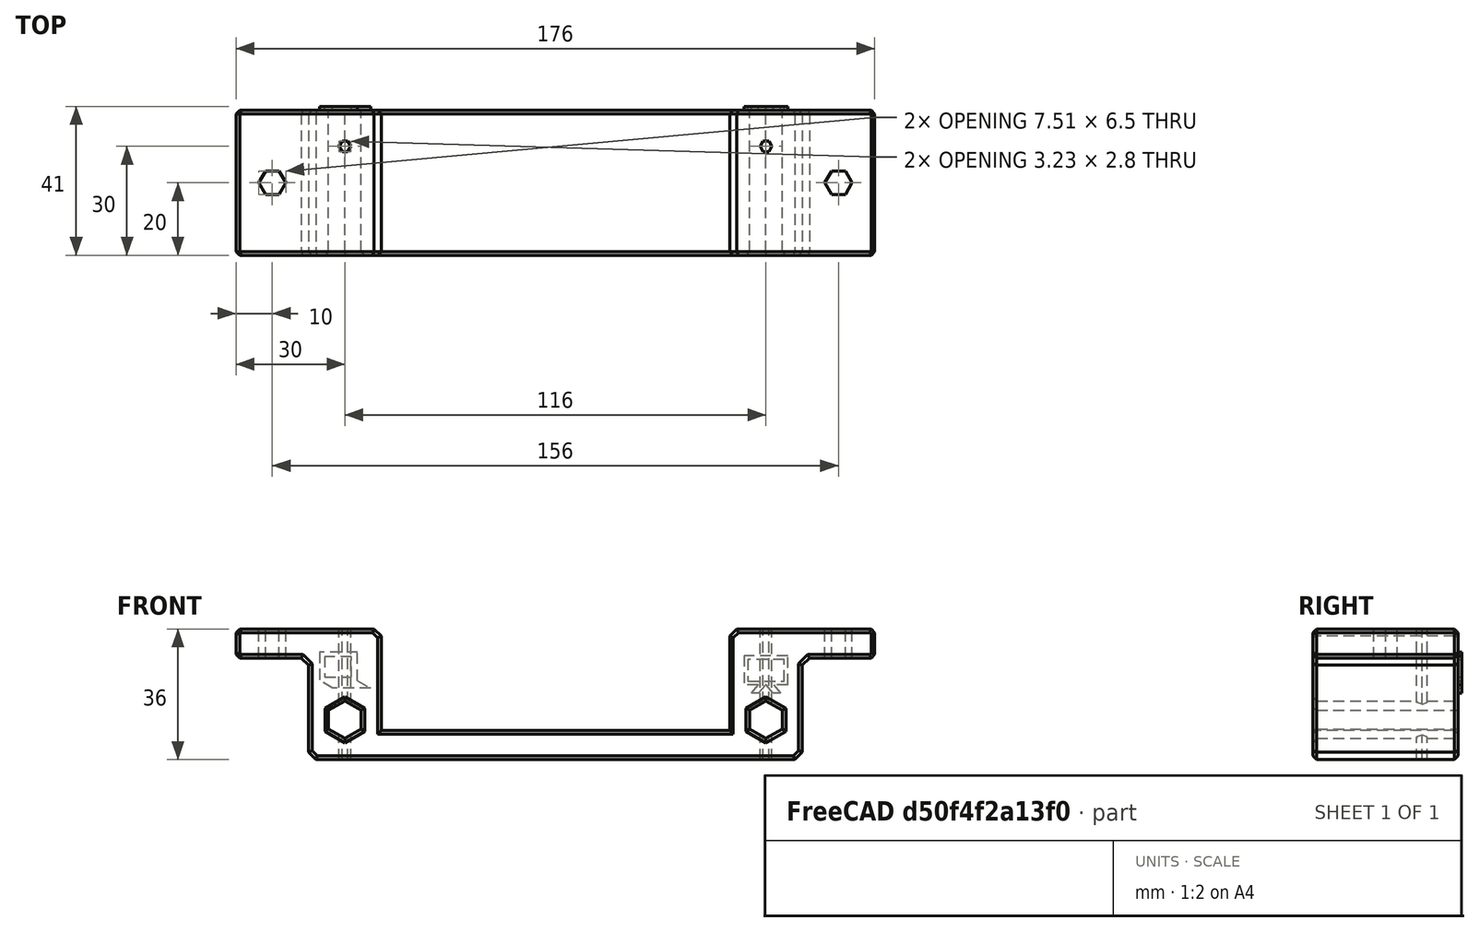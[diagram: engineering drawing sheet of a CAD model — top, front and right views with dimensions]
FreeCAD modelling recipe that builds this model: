
FCSTD DOCUMENT  (FreeCAD 0.19R)
Label: AmpClip
License: All rights reserved
LicenseURL: http://en.wikipedia.org/wiki/All_rights_reserved
objects: PartDesign::Chamfer×5, Sketcher::SketchObject×4, PartDesign::Pad×2, PartDesign::Pocket×2, PartDesign::Body×1, Mesh::Feature×1
note: 23 computed .brp shape members not serialized (recipe doc carries the construction recipe); baked Part::Feature solids carry a one-line shape summary decoded from their .brp

FEATURE [Sketcher::SketchObject] Sketch
  FullyConstrained = true
  MapMode = 5
  Placement = pos=(0,0,0) rot=(1,0,0;1.5708rad)
  Support = -> [XZ_Plane]
  sketch-geometry (12):
    g0: LineSegment StartX=-48 StartY=0 StartZ=0 EndX=-48 EndY=-28 EndZ=0
    g1: LineSegment StartX=-48 StartY=-28 StartZ=0 EndX=48 EndY=-28 EndZ=0
    g2: LineSegment StartX=48 StartY=-28 StartZ=0 EndX=48 EndY=0 EndZ=0
    g3: LineSegment StartX=48 StartY=0 StartZ=0 EndX=88 EndY=0 EndZ=0
    g4: LineSegment StartX=88 StartY=0 StartZ=0 EndX=88 EndY=-8 EndZ=0
    g5: LineSegment StartX=88 StartY=-8 StartZ=0 EndX=68 EndY=-8 EndZ=0
    g6: LineSegment StartX=68 StartY=-8 StartZ=0 EndX=68 EndY=-36 EndZ=0
    g7: LineSegment StartX=68 StartY=-36 StartZ=0 EndX=-68 EndY=-36 EndZ=0
    g8: LineSegment StartX=-68 StartY=-36 StartZ=0 EndX=-68 EndY=-8 EndZ=0
    g9: LineSegment StartX=-68 StartY=-8 StartZ=0 EndX=-88 EndY=-8 EndZ=0
    g10: LineSegment StartX=-88 StartY=-8 StartZ=0 EndX=-88 EndY=-9e-16 EndZ=0
    g11: LineSegment StartX=-88 StartY=-9e-16 StartZ=0 EndX=-48 EndY=0 EndZ=0
  constraints (32):
    c: PointOnObject(g0,g-1)
    c: Coincident(g0,g1)
    c: Horizontal(g1)
    c: Coincident(g1,g2)
    c: Vertical(g2)
    c: Coincident(g2,g3)
    c: Horizontal(g3)
    c: Coincident(g3,g4)
    c: Coincident(g4,g5)
    c: Horizontal(g5)
    c: Coincident(g5,g6)
    c: Vertical(g6)
    c: Coincident(g6,g7)
    c: Coincident(g7,g8)
    c: Coincident(g8,g9)
    c: Coincident(g9,g10)
    c: Coincident(g10,g11)
    c: Coincident(g11,g0)
    c: Horizontal(g9)
    c: Vertical(g10)
    c: Vertical(g4)
    c: Vertical(g0)
    c: Symmetric(g0,g2,g-1)
    c: Symmetric(g6,g7,g-2)
    c: Symmetric(g5,g8,g-2)
    c: Symmetric(g3,g10,g-2)
    c: Distance(g1) = 96
    c: Distance(g5,g2) = 20
    c: Distance(g4) = 8
    c: Distance(g6,g1) = 8
    c: Distance(g5) = 20
    c: Distance(g2) = 28
FEATURE [PartDesign::Pad] Pad
  Direction = (1,1,1)
  Length = 40
  Length2 = 100
  Placement = pos=(0,0,0) rot=(1,0,0;1.5708rad)
  Profile = -> Sketch
  Type = 0
FEATURE [Sketcher::SketchObject] Sketch001
  FullyConstrained = true
  MapMode = 5
  Placement = pos=(0,-40,2.66e-14) rot=(1,0,0;1.5708rad)
  Support = -> [Pad]
  sketch-geometry (14):
    g0: LineSegment StartX=62.5 StartY=-27.5981 StartZ=0 EndX=62.5 EndY=-22.4019 EndZ=0
    g1: LineSegment StartX=62.5 StartY=-22.4019 StartZ=0 EndX=58 EndY=-19.8038 EndZ=0
    g2: LineSegment StartX=58 StartY=-19.8038 StartZ=0 EndX=53.5 EndY=-22.4019 EndZ=0
    g3: LineSegment StartX=53.5 StartY=-22.4019 StartZ=0 EndX=53.5 EndY=-27.5981 EndZ=0
    g4: LineSegment StartX=53.5 StartY=-27.5981 StartZ=0 EndX=58 EndY=-30.1962 EndZ=0
    g5: LineSegment StartX=58 StartY=-30.1962 StartZ=0 EndX=62.5 EndY=-27.5981 EndZ=0
    g6: Circle CenterX=58 CenterY=-25 CenterZ=0 NormalX=0 NormalY=0 NormalZ=1 AngleXU=0 Radius=5.19615
    g7: LineSegment StartX=-58 StartY=-30.1962 StartZ=0 EndX=-53.5 EndY=-27.5981 EndZ=0
    g8: LineSegment StartX=-53.5 StartY=-27.5981 StartZ=0 EndX=-53.5 EndY=-22.4019 EndZ=0
    g9: LineSegment StartX=-53.5 StartY=-22.4019 StartZ=0 EndX=-58 EndY=-19.8038 EndZ=0
    g10: LineSegment StartX=-58 StartY=-19.8038 StartZ=0 EndX=-62.5 EndY=-22.4019 EndZ=0
    g11: LineSegment StartX=-62.5 StartY=-22.4019 StartZ=0 EndX=-62.5 EndY=-27.5981 EndZ=0
    g12: LineSegment StartX=-62.5 StartY=-27.5981 StartZ=0 EndX=-58 EndY=-30.1962 EndZ=0
    g13: Circle CenterX=-58 CenterY=-25 CenterZ=0 NormalX=0 NormalY=0 NormalZ=1 AngleXU=0 Radius=5.19615
  constraints (33):
    c: Coincident(g0,g1)
    c: Coincident(g1,g2)
    c: Coincident(g2,g3)
    c: Coincident(g3,g4)
    c: Coincident(g4,g5)
    c: Coincident(g5,g0)
    c: Equal(g0, g1-g5) x5
    c: PointOnObject(g0,g6)
    c: PointOnObject(g1,g6)
    c: PointOnObject(g2,g6)
    c: PointOnObject(g3,g6)
    c: PointOnObject(g4,g6)
    c: PointOnObject(g5,g6)
    c: Coincident(g7,g8)
    c: Coincident(g8,g9)
    c: Coincident(g9,g10)
    c: Coincident(g10,g11)
    c: Coincident(g11,g12)
    c: Coincident(g12,g7)
    c: Equal(g7, g8-g12) x5
    c: PointOnObject(g7,g13)
    c: PointOnObject(g8,g13)
    c: PointOnObject(g9,g13)
    c: PointOnObject(g10,g13)
    c: PointOnObject(g11,g13)
    c: PointOnObject(g12,g13)
    c: Distance(g7,g9) = 9
    c: Symmetric(g6,g13,g-2)
    c: Distance(g1,g3) = 9
    c: DistanceX(g6) = 58
    c: Vertical(g3)
    c: Vertical(g8)
    c: DistanceY(g6) = -25
FEATURE [PartDesign::Pocket] Pocket
  BaseFeature = -> Pad
  Length = 5
  Length2 = 100
  Placement = pos=(0,0,0) rot=(1,0,0;1.5708rad)
  Profile = -> Sketch001
  Type = 1
FEATURE [Sketcher::SketchObject] Sketch002
  FullyConstrained = true
  MapMode = 5
  Placement = pos=(0,-4e-14,-36) rot=(1,0,0;3.14159rad)
  Support = -> [Pocket]
  sketch-geometry (28):
    g0: LineSegment StartX=-57.1917 StartY=8.6 StartZ=0 EndX=-56.3834 EndY=10 EndZ=0
    g1: LineSegment StartX=-56.3834 StartY=10 StartZ=0 EndX=-57.1917 EndY=11.4 EndZ=0
    g2: LineSegment StartX=-57.1917 StartY=11.4 StartZ=0 EndX=-58.8083 EndY=11.4 EndZ=0
    g3: LineSegment StartX=-58.8083 StartY=11.4 StartZ=0 EndX=-59.6166 EndY=10 EndZ=0
    g4: LineSegment StartX=-59.6166 StartY=10 StartZ=0 EndX=-58.8083 EndY=8.6 EndZ=0
    g5: LineSegment StartX=-58.8083 StartY=8.6 StartZ=0 EndX=-57.1917 EndY=8.6 EndZ=0
    g6: Circle CenterX=-58 CenterY=10 CenterZ=0 NormalX=0 NormalY=0 NormalZ=1 AngleXU=0 Radius=1.61658
    g7: LineSegment StartX=58.8083 StartY=8.6 StartZ=0 EndX=59.6166 EndY=10 EndZ=0
    g8: LineSegment StartX=59.6166 StartY=10 StartZ=0 EndX=58.8083 EndY=11.4 EndZ=0
    g9: LineSegment StartX=58.8083 StartY=11.4 StartZ=0 EndX=57.1917 EndY=11.4 EndZ=0
    g10: LineSegment StartX=57.1917 StartY=11.4 StartZ=0 EndX=56.3834 EndY=10 EndZ=0
    g11: LineSegment StartX=56.3834 StartY=10 StartZ=0 EndX=57.1917 EndY=8.6 EndZ=0
    g12: LineSegment StartX=57.1917 StartY=8.6 StartZ=0 EndX=58.8083 EndY=8.6 EndZ=0
    g13: Circle CenterX=58 CenterY=10 CenterZ=0 NormalX=0 NormalY=0 NormalZ=1 AngleXU=0 Radius=1.61658
    g14: LineSegment StartX=-76.1236 StartY=16.75 StartZ=0 EndX=-74.2472 EndY=20 EndZ=0
    g15: LineSegment StartX=-74.2472 StartY=20 StartZ=0 EndX=-76.1236 EndY=23.25 EndZ=0
    g16: LineSegment StartX=-76.1236 StartY=23.25 StartZ=0 EndX=-79.8764 EndY=23.25 EndZ=0
    g17: LineSegment StartX=-79.8764 StartY=23.25 StartZ=0 EndX=-81.7528 EndY=20 EndZ=0
    g18: LineSegment StartX=-81.7528 StartY=20 StartZ=0 EndX=-79.8764 EndY=16.75 EndZ=0
    g19: LineSegment StartX=-79.8764 StartY=16.75 StartZ=0 EndX=-76.1236 EndY=16.75 EndZ=0
    g20: Circle CenterX=-78 CenterY=20 CenterZ=0 NormalX=0 NormalY=0 NormalZ=1 AngleXU=0 Radius=3.75278
    g21: LineSegment StartX=79.8764 StartY=16.75 StartZ=0 EndX=81.7528 EndY=20 EndZ=0
    g22: LineSegment StartX=81.7528 StartY=20 StartZ=0 EndX=79.8764 EndY=23.25 EndZ=0
    g23: LineSegment StartX=79.8764 StartY=23.25 StartZ=0 EndX=76.1236 EndY=23.25 EndZ=0
    g24: LineSegment StartX=76.1236 StartY=23.25 StartZ=0 EndX=74.2472 EndY=20 EndZ=0
    g25: LineSegment StartX=74.2472 StartY=20 StartZ=0 EndX=76.1236 EndY=16.75 EndZ=0
    g26: LineSegment StartX=76.1236 StartY=16.75 StartZ=0 EndX=79.8764 EndY=16.75 EndZ=0
    g27: Circle CenterX=78 CenterY=20 CenterZ=0 NormalX=0 NormalY=0 NormalZ=1 AngleXU=0 Radius=3.75278
  constraints (66):
    c: Coincident(g0,g1)
    c: Coincident(g1,g2)
    c: Coincident(g2,g3)
    c: Coincident(g3,g4)
    c: Coincident(g4,g5)
    c: Coincident(g5,g0)
    c: Equal(g0, g1-g5) x5
    c: PointOnObject(g0,g6)
    c: PointOnObject(g1,g6)
    c: PointOnObject(g2,g6)
    c: PointOnObject(g3,g6)
    c: PointOnObject(g4,g6)
    c: PointOnObject(g5,g6)
    c: Coincident(g7,g8)
    c: Coincident(g8,g9)
    c: Coincident(g9,g10)
    c: Coincident(g10,g11)
    c: Coincident(g11,g12)
    c: Coincident(g12,g7)
    c: Equal(g7, g8-g12) x5
    c: PointOnObject(g7,g13)
    c: PointOnObject(g8,g13)
    c: PointOnObject(g9,g13)
    c: PointOnObject(g10,g13)
    c: PointOnObject(g11,g13)
    c: PointOnObject(g12,g13)
    c: Horizontal(g9)
    c: Horizontal(g2)
    c: DistanceX(g-1,g13) = 58
    c: Symmetric(g13,g6,g-2)
    c: DistanceY(g6) = 10
    c: Distance(g1,g3) = 2.8
    c: Equal(g11,g2)
    c: Coincident(g14,g15)
    c: Coincident(g15,g16)
    c: Coincident(g16,g17)
    c: Coincident(g17,g18)
    c: Coincident(g18,g19)
    c: Coincident(g19,g14)
    c: Equal(g14, g15-g19) x5
    c: PointOnObject(g14,g20)
    c: PointOnObject(g15,g20)
    c: PointOnObject(g16,g20)
    c: PointOnObject(g17,g20)
    c: PointOnObject(g18,g20)
    c: PointOnObject(g19,g20)
    c: Coincident(g21,g22)
    c: Coincident(g22,g23)
    c: Coincident(g23,g24)
    c: Coincident(g24,g25)
    c: Coincident(g25,g26)
    c: Coincident(g26,g21)
    c: Equal(g21, g22-g26) x5
    c: PointOnObject(g21,g27)
    c: PointOnObject(g22,g27)
    c: PointOnObject(g23,g27)
    c: PointOnObject(g24,g27)
    c: PointOnObject(g25,g27)
    c: PointOnObject(g26,g27)
    c: Symmetric(g27,g20,g-2)
    c: Distance(g14,g16) = 6.5
    c: DistanceX(g20) = -78
    c: Horizontal(g16)
    c: Horizontal(g23)
    c: DistanceY(g27) = 20
    c: Equal(g23,g16)
FEATURE [PartDesign::Pocket] Pocket001
  BaseFeature = -> Pocket
  Length = 5
  Length2 = 100
  Placement = pos=(0,0,0) rot=(1,0,0;1.5708rad)
  Profile = -> Sketch002
  Type = 1
FEATURE [PartDesign::Chamfer] Chamfer
  Angle = 45
  Base = -> Pocket001 [Edge122,Edge109,Edge107,Edge93]
  BaseFeature = -> Pocket001
  ChamferType = 0
  FlipDirection = false
  Placement = pos=(0,0,0) rot=(1,0,0;1.5708rad)
  Size = 2
  Size2 = 1
  SupportTransform = false
FEATURE [PartDesign::Chamfer] Chamfer001
  Angle = 45
  Base = -> Chamfer [Edge80,Edge45]
  BaseFeature = -> Chamfer
  ChamferType = 0
  FlipDirection = false
  Placement = pos=(0,0,0) rot=(1,0,0;1.5708rad)
  Size = 2
  Size2 = 1
  SupportTransform = false
FEATURE [PartDesign::Chamfer] Chamfer002
  Angle = 45
  Base = -> Chamfer001 [Edge100,Edge72,Edge32,Edge48]
  BaseFeature = -> Chamfer001
  ChamferType = 0
  FlipDirection = false
  Placement = pos=(0,0,0) rot=(1,0,0;1.5708rad)
  Size = 1
  Size2 = 1
  SupportTransform = false
FEATURE [PartDesign::Chamfer] Chamfer003
  Angle = 45
  Base = -> Chamfer002 [Face36]
  BaseFeature = -> Chamfer002
  ChamferType = 0
  FlipDirection = false
  Placement = pos=(0,0,0) rot=(1,0,0;1.5708rad)
  Size = 1
  Size2 = 1
  SupportTransform = false
FEATURE [Sketcher::SketchObject] Sketch003
  FullyConstrained = false
  MapMode = 5
  Placement = pos=(0,0,0) rot=(-1,0,0;1.5708rad)
  Support = -> [Chamfer003]
  sketch-geometry (26):
    g0: LineSegment StartX=-56.1799 StartY=7.5908 StartZ=0 EndX=-63.5196 EndY=7.5908 EndZ=0
    g1: LineSegment StartX=-63.5196 StartY=7.5908 StartZ=0 EndX=-63.5196 EndY=13.2807 EndZ=0
    g2: LineSegment StartX=-63.5196 StartY=13.2807 StartZ=0 EndX=-56.1799 EndY=13.2807 EndZ=0
    g3: LineSegment StartX=-56.1799 StartY=13.2807 StartZ=0 EndX=-56.1799 EndY=7.5908 EndZ=0
    g4: LineSegment StartX=-54.5116 StartY=6.37856 StartZ=0 EndX=-65.0116 EndY=6.37856 EndZ=0
    g5: LineSegment StartX=-65.0116 StartY=6.37856 StartZ=0 EndX=-65.0116 EndY=14.2092 EndZ=0
    g6: LineSegment StartX=-54.5116 StartY=14.2092 StartZ=0 EndX=-54.5116 EndY=6.37856 EndZ=0
    g7: LineSegment StartX=-54.5116 StartY=14.2092 StartZ=0 EndX=-50.9031 EndY=16.3184 EndZ=0
    g8: LineSegment StartX=-50.9031 StartY=16.3184 StartZ=0 EndX=-61.4031 EndY=16.3184 EndZ=0
    g9: LineSegment StartX=-61.4031 StartY=16.3184 StartZ=0 EndX=-65.0116 EndY=14.2092 EndZ=0
    g10: LineSegment StartX=64.0151 StartY=7.35586 StartZ=0 EndX=52.0151 EndY=7.35586 EndZ=0
    g11: LineSegment StartX=52.0151 StartY=7.35586 StartZ=0 EndX=52.0151 EndY=15.3559 EndZ=0
    g12: LineSegment StartX=64.0151 StartY=15.3559 StartZ=0 EndX=64.0151 EndY=7.35586 EndZ=0
    g13: LineSegment StartX=63.0151 StartY=8.35586 StartZ=0 EndX=53.0151 EndY=8.35586 EndZ=0
    g14: LineSegment StartX=53.0151 StartY=8.35586 StartZ=0 EndX=53.0151 EndY=14.3559 EndZ=0
    g15: LineSegment StartX=53.0151 StartY=14.3559 StartZ=0 EndX=63.0151 EndY=14.3559 EndZ=0
    g16: LineSegment StartX=63.0151 StartY=14.3559 StartZ=0 EndX=63.0151 EndY=8.35586 EndZ=0
    g17: LineSegment StartX=64.0151 StartY=15.3559 StartZ=0 EndX=60.1151 EndY=15.3559 EndZ=0
    g18: LineSegment StartX=60.1151 StartY=15.3559 StartZ=0 EndX=62.0434 EndY=17.654 EndZ=0
    g19: LineSegment StartX=62.0434 StartY=17.654 StartZ=0 EndX=60.0434 EndY=17.654 EndZ=0
    g20: LineSegment StartX=60.0434 StartY=17.654 StartZ=0 EndX=58.1151 EndY=15.3559 EndZ=0
    g21: LineSegment StartX=58.1151 StartY=15.3559 StartZ=0 EndX=57.9151 EndY=15.3559 EndZ=0
    g22: LineSegment StartX=57.9151 StartY=15.3559 StartZ=0 EndX=55.9867 EndY=17.654 EndZ=0
    g23: LineSegment StartX=55.9867 StartY=17.654 StartZ=0 EndX=53.9867 EndY=17.654 EndZ=0
    g24: LineSegment StartX=53.9867 StartY=17.654 StartZ=0 EndX=55.9151 EndY=15.3559 EndZ=0
    g25: LineSegment StartX=55.9151 StartY=15.3559 StartZ=0 EndX=52.0151 EndY=15.3559 EndZ=0
  constraints (67):
    c: Coincident(g0,g1)
    c: Coincident(g1,g2)
    c: Coincident(g2,g3)
    c: Coincident(g3,g0)
    c: Horizontal(g0)
    c: Horizontal(g2)
    c: Vertical(g1)
    c: Vertical(g3)
    c: Coincident(g4,g5)
    c: Coincident(g6,g4)
    c: Horizontal(g4)
    c: Vertical(g5)
    c: Vertical(g6)
    c: Coincident(g6,g7)
    c: Coincident(g7,g8)
    c: Horizontal(g8)
    c: Coincident(g8,g9)
    c: Coincident(g9,g5)
    c: Parallel(g7,g9)
    c: DistanceY(g5,g6) = 0
    c: Coincident(g10,g11)
    c: Coincident(g12,g10)
    c: Horizontal(g10)
    c: Vertical(g11)
    c: Vertical(g12)
    c: Distance(g4) = 10.5
    c: Coincident(g13,g14)
    c: Coincident(g14,g15)
    c: Coincident(g15,g16)
    c: Coincident(g16,g13)
    c: Horizontal(g13)
    c: Horizontal(g15)
    c: Vertical(g14)
    c: Vertical(g16)
    c: Coincident(g12,g17)
    c: Horizontal(g17)
    c: Coincident(g17,g18)
    c: Coincident(g18,g19)
    c: Horizontal(g19)
    c: Coincident(g19,g20)
    c: Coincident(g20,g21)
    c: Coincident(g21,g22)
    c: Coincident(g22,g23)
    c: Coincident(g23,g24)
    c: Coincident(g24,g25)
    c: Coincident(g25,g11)
    c: Horizontal(g25)
    c: Equal(g25,g17)
    c: Equal(g23,g19)
    c: Equal(g20,g22)
    c: Parallel(g20,g18)
    c: Parallel(g22,g24)
    c: Horizontal(g21)
    c: Horizontal(g23)
    c: Angle(g24) = -0.872665
    c: Angle(g18) = 0.872665
    c: Distance(g19) = 2
    c: DistanceY(g17,g20) = 0
    c: DistanceY(g24,g21) = 0
    c: Distance(g10) = 12
    c: Distance(g13) = 10
    c: Distance(g14) = 6
    c: Distance(g11) = 8
    c: Distance(g22) = 3
    c: Distance(g14,g25) = 1
    c: Distance(g14,g11) = 1
    c: Distance(g21) = 0.2
FEATURE [PartDesign::Pad] Pad001
  BaseFeature = -> Chamfer003
  Direction = (1,1,1)
  Length = 1
  Length2 = 100
  Placement = pos=(0,0,0) rot=(1,0,0;1.5708rad)
  Profile = -> Sketch003
  Type = 0
FEATURE [PartDesign::Chamfer] Chamfer004
  Angle = 45
  Base = -> Pad001 [Edge36,Edge38,Edge40,Edge34,Edge32,Edge30,Edge28,Edge26,Edge24,Edge18,Edge3,Edge23,Edge25,Edge27,Edge29,Edge31,Edge33,Edge42,Edge41,Edge39,Edge37,Edge35]
  BaseFeature = -> Pad001
  ChamferType = 0
  FlipDirection = false
  Placement = pos=(0,0,0) rot=(1,0,0;1.5708rad)
  Size = 1
  Size2 = 1
  SupportTransform = false
FEATURE [PartDesign::Body] Body
  Group = -> [Sketch,Pad,Sketch001,Pocket,Sketch002,Pocket001,Chamfer,Chamfer001,Chamfer002,Chamfer003,Sketch003,Pad001,Chamfer004]
  Origin = -> Origin
  Tip = -> Chamfer004
FEATURE [Mesh::Feature] Mesh  label="Chamfer004 (Meshed)"
